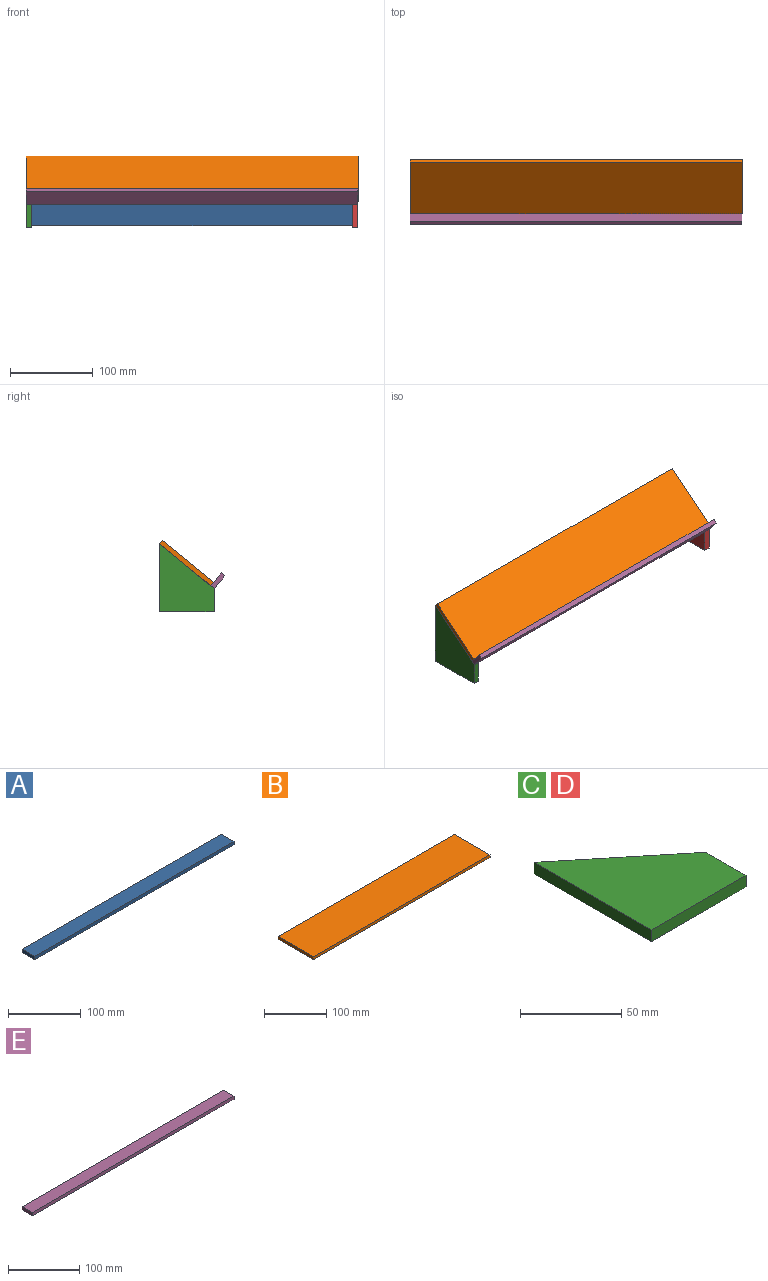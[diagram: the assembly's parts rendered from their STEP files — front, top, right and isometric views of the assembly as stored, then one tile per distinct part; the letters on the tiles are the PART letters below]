
ASSEMBLY  parts=5 mates=5
PART A: 6 faces, bbox 386x25x5.5 mm
  f0: plane 386x5.5mm, normal (0,-1,0), area 2123mm2, adj f1,f3,f4,f5
  f1: plane 25x5.5mm, normal (1,0,0), area 137.5mm2, adj f0,f2,f4,f5
  f2: plane 386x5.5mm, normal (0,1,0), area 2123mm2, adj f1,f3,f4,f5
  f3: plane 25x5.5mm, normal (-1,0,0), area 137.5mm2, adj f0,f2,f4,f5
  f4: plane 386x25mm, normal (0,0,1), area 9650mm2, adj f0,f1,f2,f3
  f5: plane 386x25mm, normal (0,0,-1), area 9650mm2, adj f0,f1,f2,f3
PART B: 6 faces, bbox 400x80x5.5 mm
  f0: plane 400x5.5mm, normal (0,-1,0), area 2200mm2, adj f1,f3,f4,f5
  f1: plane 80x5.5mm, normal (1,0,0), area 440mm2, adj f0,f2,f4,f5
  f2: plane 400x5.5mm, normal (0,1,0), area 2200mm2, adj f1,f3,f4,f5
  f3: plane 80x5.5mm, normal (-1,0,0), area 440mm2, adj f0,f2,f4,f5
  f4: plane 400x80mm, normal (0,0,1), area 32000mm2, adj f0,f1,f2,f3
  f5: plane 400x80mm, normal (0,0,-1), area 32000mm2, adj f0,f1,f2,f3
PART C: 6 faces, bbox 66.2x82.1x7 mm
  f0: plane 82.06x7mm, normal (-1,0,0), area 574.4mm2, adj f1,f3,f4,f5
  f1: plane 66.24x7mm, normal (0,-1,0), area 463.7mm2, adj f0,f2,f4,f5
  f2: plane 28x7mm, normal (1,0,0), area 196mm2, adj f1,f3,f4,f5
  f3: plane 66.24x54.06mm, normal (0.63,0.77,0), area 598.5mm2, adj f0,f2,f4,f5
  f4: plane 82.06x66.24mm, normal (0,0,1), area 3645.3mm2, adj f0,f1,f2,f3
  f5: plane 82.06x66.24mm, normal (0,0,-1), area 3645.3mm2, adj f0,f1,f2,f3
PART D: same geometry as C
PART E: 6 faces, bbox 400x20x5.5 mm
  f0: plane 400x5.5mm, normal (0,-1,0), area 2200mm2, adj f1,f3,f4,f5
  f1: plane 20x5.5mm, normal (1,0,0), area 110mm2, adj f0,f2,f4,f5
  f2: plane 400x5.5mm, normal (0,1,0), area 2200mm2, adj f1,f3,f4,f5
  f3: plane 20x5.5mm, normal (-1,0,0), area 110mm2, adj f0,f2,f4,f5
  f4: plane 400x20mm, normal (0,0,1), area 8000mm2, adj f0,f1,f2,f3
  f5: plane 400x20mm, normal (0,0,-1), area 8000mm2, adj f0,f1,f2,f3
PLACE A rot(axis=(-1,0,0),90deg) t=(404.74,-54.44,-42.17)mm
PLACE B rot(axis=(1,0,0),39.2deg) t=(404.74,-76.88,-0.57)mm
PLACE C rot(axis=(0.58,-0.58,-0.58),120deg) t=(211.74,-45.69,-57.17)mm
PLACE D rot(axis=(0.58,-0.58,-0.58),120deg) t=(604.74,-45.69,-57.17)mm
PLACE E rot(axis=(1,0,0),129.2deg) t=(404.74,-114.19,-18.11)mm
MATE fastened B.f0 <-> E.f5  axis (0,-0.77,-0.63) through (404.74,-107.87,-25.86)mm
MATE fastened C.f5 <-> A.f3  axis (-1,0,0) through (211.74,-45.69,-57.17)mm
MATE parallel C.f4 <-> D.f4  axis (-1,0,0) through (204.74,-73.39,-27.45)mm
MATE fastened D.f4 <-> A.f1  axis (-1,0,0) through (597.74,-45.69,-57.17)mm
MATE fastened B.f5 <-> C.f3  axis (0,0.63,-0.77) through (204.74,-78.82,-2.15)mm
